# Revit family: result
name_source: partatom
category: Plumbing Fixtures
revit_build: Autodesk Revit 2015 (Build: 20140903_1530(x64)
units: mm (PartAtom-declared; Revit-internal decimal feet)

## types (1)
- Default
    BIMobject category = Toilet Accessories
    BIMobject category code = sanitary-toilet-accessories
    BIMobject main category = Sanitary
    BIMobject main category code = sanitary
    Brand url = http://www.hansgrohe-int.com
    Design country = Germany
    Edition number = 1
    GTIN code = https://4059625203538
    IFC Classification = Object
    Installation instructions = https://www.hansgrohe-usa.com
    Manufacturer country = Germany
    Manufacturer name = hansgrohe
    Masterformat 2014 Code = 01 52 19
    Masterformat 2014 Description = Sanitary Facilities
    NBS Reference Code = 31-75
    NBS Reference Description = Sanitary Accessories
    OmniClass Code = 23-31 25 21
    OmniClass Description = Toilet Paper Dispensers
    Product Guid = c5338edf-ad5b-41e3-b81f-57f17bdc9076
    Product SKU = 04787830
    Product data url = https://bimobject.com
    Product family = Joleena
    Product group = Roll holders
    Product name = 04787830 Joleena Roll holder
    Product url = https://www.hansgrohe-usa.com
    QR code = http://bimobject.com
    Technical description = https://www.hansgrohe-usa.com
    UNSPSC Code = 301815
    Uniclass 1.4 Code = L8244
    Uniclass 1.4 Description = Sanitary dispensers
    Uniclass 2.0 Code = PR-31-75
    Uniclass 2.0 Description = Sanitary Accessories
    Uniclass 2015 Code = Pr_40_70_22_90
    Uniclass 2015 Name = Toilet paper dispensers
    Uniformat II Code = E1090
    Uniformat II Description = Other Equipment

## geometry (parser evidence)
native form markers: Sweep x3
no freeform markers — native parametric forms only
